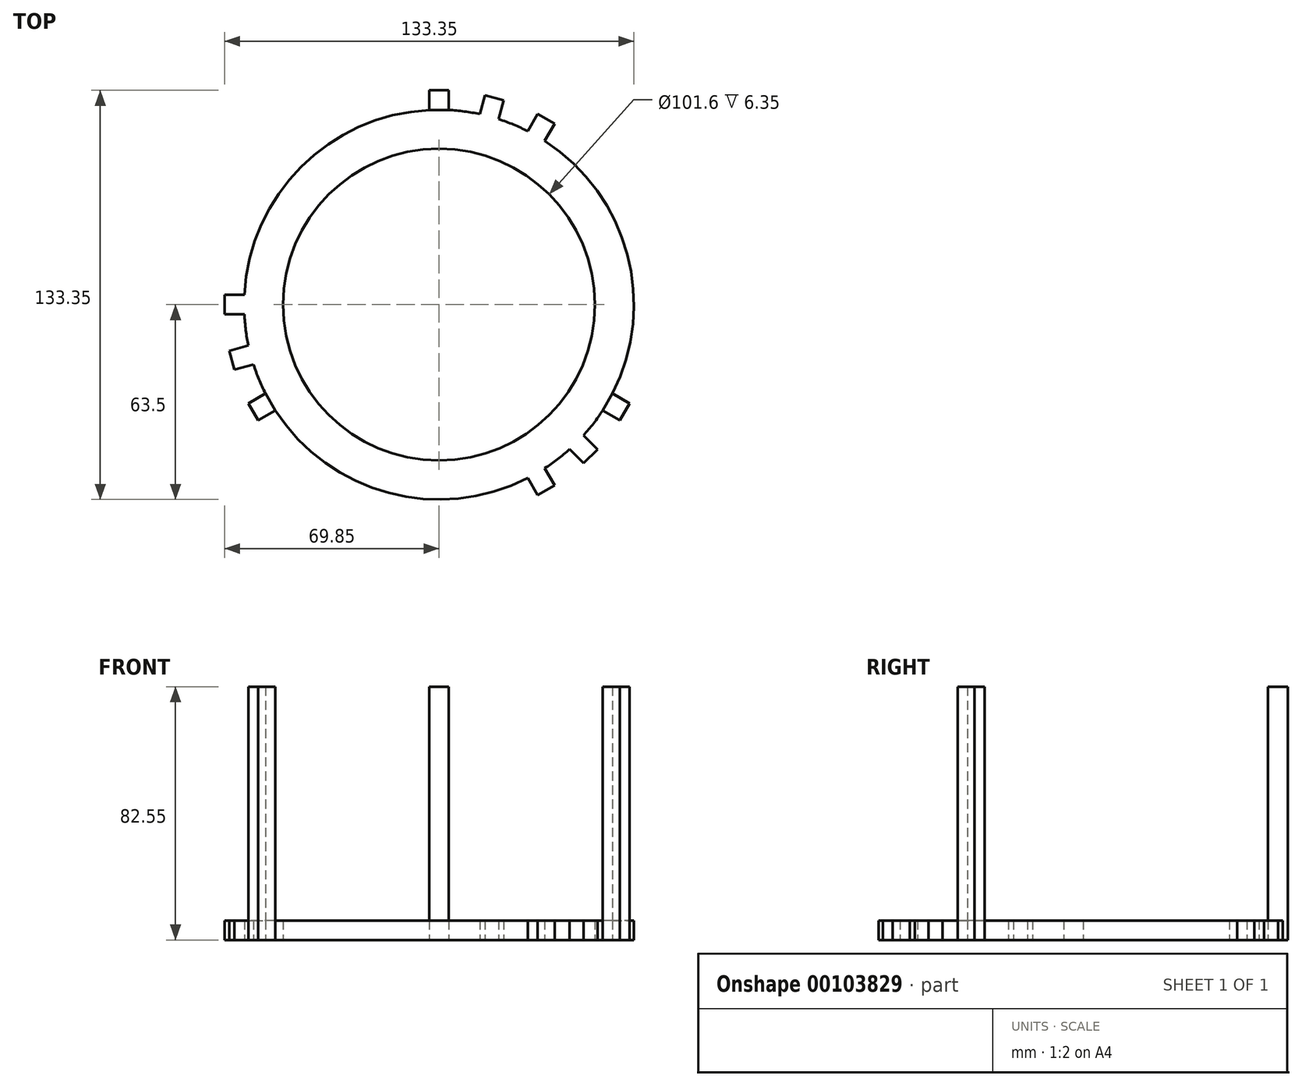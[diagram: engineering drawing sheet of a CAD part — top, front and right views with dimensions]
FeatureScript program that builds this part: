
annotation { "Feature Type Name" : "Feature", "Feature Type Description" : "" }
export const myFeature = defineFeature(function(context is Context, id is Id, definition is map)
    precondition{}
    {
        {
            var Q0;
            Q0=qCreatedBy(makeId("Top.planeOp"),FACE);
            var sketch = newSketch(context, id + "F0", { "sketchPlane" : qUnion([Q0])});
            skCircle(sketch, "E0", {"center": v(0, 0) * mm, "radius": 50.8 * mm});
            skCircle(sketch, "E1", {"center": v(0, 0) * mm, "radius": 63.5 * mm});
            skLineSegment(sketch, "E2.bottom", {"start": v(3.18, 69.85) * mm, "end": v(-3.17, 69.85) * mm});
            skLineSegment(sketch, "E2.top", {"start": v(3.18, 57.15) * mm, "end": v(-3.17, 57.15) * mm});
            skLineSegment(sketch, "E2.left", {"start": v(3.18, 69.85) * mm, "end": v(3.18, 57.15) * mm});
            skLineSegment(sketch, "E2.right", {"start": v(-3.17, 69.85) * mm, "end": v(-3.17, 57.15) * mm});
            skPoint(sketch, "E2.middle", {"position": v(0, 63.5) * mm});
            skLineSegment(sketch, "E3.1.0", {"start": v(21.15, 66.65) * mm, "end": v(15.01, 68.3) * mm});
            skLineSegment(sketch, "E3.1.1", {"start": v(21.15, 66.65) * mm, "end": v(17.86, 54.38) * mm});
            skLineSegment(sketch, "E3.1.2", {"start": v(17.86, 54.38) * mm, "end": v(11.72, 56.02) * mm});
            skLineSegment(sketch, "E3.1.3", {"start": v(15.01, 68.3) * mm, "end": v(11.72, 56.02) * mm});
            skLineSegment(sketch, "E3.2.0", {"start": v(37.67, 58.9) * mm, "end": v(32.18, 62.08) * mm});
            skLineSegment(sketch, "E3.2.1", {"start": v(37.67, 58.9) * mm, "end": v(31.32, 47.9) * mm});
            skLineSegment(sketch, "E3.2.2", {"start": v(31.32, 47.9) * mm, "end": v(25.83, 51.08) * mm});
            skLineSegment(sketch, "E3.2.3", {"start": v(32.18, 62.08) * mm, "end": v(25.83, 51.08) * mm});
            skLineSegment(sketch, "E3.anchor1", {"start": v(0, 0) * mm, "end": v(-3.17, 69.85) * mm, "construction": true});
            skLineSegment(sketch, "E3.anchor2", {"start": v(0, 0) * mm, "end": v(32.18, 62.08) * mm, "construction": true});
            skLineSegment(sketch, "E4.1.0", {"start": v(-69.85, 3.18) * mm, "end": v(-57.15, 3.18) * mm});
            skLineSegment(sketch, "E4.1.1", {"start": v(-69.85, 3.18) * mm, "end": v(-69.85, -3.17) * mm});
            skLineSegment(sketch, "E4.1.2", {"start": v(-57.15, 3.18) * mm, "end": v(-57.15, -3.17) * mm});
            skLineSegment(sketch, "E4.1.3", {"start": v(-69.85, -3.17) * mm, "end": v(-57.15, -3.17) * mm});
            skLineSegment(sketch, "E4.1.4", {"start": v(-68.3, -15.01) * mm, "end": v(-56.02, -11.72) * mm});
            skLineSegment(sketch, "E4.1.5", {"start": v(-68.3, -15.01) * mm, "end": v(-66.65, -21.15) * mm});
            skLineSegment(sketch, "E4.1.6", {"start": v(-56.02, -11.72) * mm, "end": v(-54.38, -17.86) * mm});
            skLineSegment(sketch, "E4.1.7", {"start": v(-66.65, -21.15) * mm, "end": v(-54.38, -17.86) * mm});
            skLineSegment(sketch, "E4.1.8", {"start": v(-62.08, -32.18) * mm, "end": v(-51.08, -25.83) * mm});
            skLineSegment(sketch, "E4.1.9", {"start": v(-62.08, -32.18) * mm, "end": v(-58.9, -37.67) * mm});
            skLineSegment(sketch, "E4.1.10", {"start": v(-58.9, -37.67) * mm, "end": v(-47.9, -31.32) * mm});
            skLineSegment(sketch, "E4.1.11", {"start": v(-51.08, -25.83) * mm, "end": v(-47.9, -31.32) * mm});
            skLineSegment(sketch, "E4.2.0", {"start": v(32.18, -62.08) * mm, "end": v(25.83, -51.08) * mm});
            skLineSegment(sketch, "E4.2.1", {"start": v(32.18, -62.08) * mm, "end": v(37.67, -58.9) * mm});
            skLineSegment(sketch, "E4.2.2", {"start": v(25.83, -51.08) * mm, "end": v(31.32, -47.9) * mm});
            skLineSegment(sketch, "E4.2.3", {"start": v(37.67, -58.9) * mm, "end": v(31.32, -47.9) * mm});
            skLineSegment(sketch, "E4.2.4", {"start": v(47.15, -51.64) * mm, "end": v(38.17, -42.66) * mm});
            skLineSegment(sketch, "E4.2.5", {"start": v(47.15, -51.64) * mm, "end": v(51.64, -47.15) * mm});
            skLineSegment(sketch, "E4.2.6", {"start": v(38.17, -42.66) * mm, "end": v(42.66, -38.17) * mm});
            skLineSegment(sketch, "E4.2.7", {"start": v(51.64, -47.15) * mm, "end": v(42.66, -38.17) * mm});
            skLineSegment(sketch, "E4.2.8", {"start": v(58.9, -37.67) * mm, "end": v(47.9, -31.32) * mm});
            skLineSegment(sketch, "E4.2.9", {"start": v(58.9, -37.67) * mm, "end": v(62.08, -32.18) * mm});
            skLineSegment(sketch, "E4.2.10", {"start": v(62.08, -32.18) * mm, "end": v(51.08, -25.83) * mm});
            skLineSegment(sketch, "E4.2.11", {"start": v(47.9, -31.32) * mm, "end": v(51.08, -25.83) * mm});
            skSolve(sketch);
        }
        {
            var Q0;
            Q0=makeQuery(id+"F0.imprint","IMPRINT",FACE,{"disambiguationData":[TD([[makeQuery(id+"F0.imprint","IMPRINT",EDGE,{"derivedFrom":sQuery(id+"F0.wireOp",EDGE,"E0")}),-1.0]])]});
            var Q1;
            {var subQ5=sQuery(id+"F0.wireOp",EDGE,"fd1a7b6d-0c8d-4171-9b3e-83a91182237e.1.1");Q1=makeQuery(id+"F0.imprint","IMPRINT",FACE,{"disambiguationData":[TD([[makeQuery(id+"F0.imprint","IMPRINT",EDGE,{"derivedFrom":subQ5}),1.0]])]});}
            var Q2;
            {var subQ5=sQuery(id+"F0.wireOp",EDGE,"fd1a7b6d-0c8d-4171-9b3e-83a91182237e.1.3");Q2=makeQuery(id+"F0.imprint","IMPRINT",FACE,{"disambiguationData":[TD([[makeQuery(id+"F0.imprint","IMPRINT",EDGE,{"derivedFrom":subQ5}),-1.0]])]});}
            var Q3;
            {var subQ5=sQuery(id+"F0.wireOp",EDGE,"E2.bottom");Q3=makeQuery(id+"F0.imprint","IMPRINT",FACE,{"disambiguationData":[TD([[makeQuery(id+"F0.imprint","IMPRINT",EDGE,{"derivedFrom":subQ5}),1.0]])]});}
            var Q4;
            {var subQ5=sQuery(id+"F0.wireOp",EDGE,"E2.top");Q4=makeQuery(id+"F0.imprint","IMPRINT",FACE,{"disambiguationData":[TD([[makeQuery(id+"F0.imprint","IMPRINT",EDGE,{"derivedFrom":subQ5}),-1.0]])]});}
            var Q5;
            {var subQ5=sQuery(id+"F0.wireOp",EDGE,"fd1a7b6d-0c8d-4171-9b3e-83a91182237e.2.1");Q5=makeQuery(id+"F0.imprint","IMPRINT",FACE,{"disambiguationData":[TD([[makeQuery(id+"F0.imprint","IMPRINT",EDGE,{"derivedFrom":subQ5}),1.0]])]});}
            var Q6;
            {var subQ5=sQuery(id+"F0.wireOp",EDGE,"fd1a7b6d-0c8d-4171-9b3e-83a91182237e.2.3");Q6=makeQuery(id+"F0.imprint","IMPRINT",FACE,{"disambiguationData":[TD([[makeQuery(id+"F0.imprint","IMPRINT",EDGE,{"derivedFrom":subQ5}),-1.0]])]});}
            var Q7;
            {var subQ5=sQuery(id+"F0.wireOp",EDGE,"E3.1.2");Q7=makeQuery(id+"F0.imprint","IMPRINT",FACE,{"disambiguationData":[TD([[makeQuery(id+"F0.imprint","IMPRINT",EDGE,{"derivedFrom":subQ5}),-1.0]])]});}
            var Q8;
            {var subQ5=sQuery(id+"F0.wireOp",EDGE,"E3.1.0");Q8=makeQuery(id+"F0.imprint","IMPRINT",FACE,{"disambiguationData":[TD([[makeQuery(id+"F0.imprint","IMPRINT",EDGE,{"derivedFrom":subQ5}),1.0]])]});}
            var Q9;
            {var subQ5=sQuery(id+"F0.wireOp",EDGE,"E3.2.0");Q9=makeQuery(id+"F0.imprint","IMPRINT",FACE,{"disambiguationData":[TD([[makeQuery(id+"F0.imprint","IMPRINT",EDGE,{"derivedFrom":subQ5}),1.0]])]});}
            var Q10;
            {var subQ5=sQuery(id+"F0.wireOp",EDGE,"E3.2.2");Q10=makeQuery(id+"F0.imprint","IMPRINT",FACE,{"disambiguationData":[TD([[makeQuery(id+"F0.imprint","IMPRINT",EDGE,{"derivedFrom":subQ5}),-1.0]])]});}
            var Q11;
            {var subQ5=sQuery(id+"F0.wireOp",EDGE,"E4.2.9");Q11=makeQuery(id+"F0.imprint","IMPRINT",FACE,{"disambiguationData":[TD([[makeQuery(id+"F0.imprint","IMPRINT",EDGE,{"derivedFrom":subQ5}),1.0]])]});}
            var Q12;
            {var subQ5=sQuery(id+"F0.wireOp",EDGE,"E4.2.11");Q12=makeQuery(id+"F0.imprint","IMPRINT",FACE,{"disambiguationData":[TD([[makeQuery(id+"F0.imprint","IMPRINT",EDGE,{"derivedFrom":subQ5}),-1.0]])]});}
            var Q13;
            {var subQ5=sQuery(id+"F0.wireOp",EDGE,"E4.2.5");Q13=makeQuery(id+"F0.imprint","IMPRINT",FACE,{"disambiguationData":[TD([[makeQuery(id+"F0.imprint","IMPRINT",EDGE,{"derivedFrom":subQ5}),1.0]])]});}
            var Q14;
            {var subQ5=sQuery(id+"F0.wireOp",EDGE,"E4.2.6");Q14=makeQuery(id+"F0.imprint","IMPRINT",FACE,{"disambiguationData":[TD([[makeQuery(id+"F0.imprint","IMPRINT",EDGE,{"derivedFrom":subQ5}),-1.0]])]});}
            var Q15;
            {var subQ5=sQuery(id+"F0.wireOp",EDGE,"E4.2.2");Q15=makeQuery(id+"F0.imprint","IMPRINT",FACE,{"disambiguationData":[TD([[makeQuery(id+"F0.imprint","IMPRINT",EDGE,{"derivedFrom":subQ5}),-1.0]])]});}
            var Q16;
            {var subQ5=sQuery(id+"F0.wireOp",EDGE,"E4.2.1");Q16=makeQuery(id+"F0.imprint","IMPRINT",FACE,{"disambiguationData":[TD([[makeQuery(id+"F0.imprint","IMPRINT",EDGE,{"derivedFrom":subQ5}),1.0]])]});}
            var Q17;
            {var subQ5=sQuery(id+"F0.wireOp",EDGE,"E4.1.9");Q17=makeQuery(id+"F0.imprint","IMPRINT",FACE,{"disambiguationData":[TD([[makeQuery(id+"F0.imprint","IMPRINT",EDGE,{"derivedFrom":subQ5}),1.0]])]});}
            var Q18;
            {var subQ5=sQuery(id+"F0.wireOp",EDGE,"E4.1.5");Q18=makeQuery(id+"F0.imprint","IMPRINT",FACE,{"disambiguationData":[TD([[makeQuery(id+"F0.imprint","IMPRINT",EDGE,{"derivedFrom":subQ5}),1.0]])]});}
            var Q19;
            {var subQ5=sQuery(id+"F0.wireOp",EDGE,"E4.1.1");Q19=makeQuery(id+"F0.imprint","IMPRINT",FACE,{"disambiguationData":[TD([[makeQuery(id+"F0.imprint","IMPRINT",EDGE,{"derivedFrom":subQ5}),1.0]])]});}
            var Q20;
            {var subQ5=sQuery(id+"F0.wireOp",EDGE,"E4.1.2");Q20=makeQuery(id+"F0.imprint","IMPRINT",FACE,{"disambiguationData":[TD([[makeQuery(id+"F0.imprint","IMPRINT",EDGE,{"derivedFrom":subQ5}),-1.0]])]});}
            var Q21;
            {var subQ5=sQuery(id+"F0.wireOp",EDGE,"E4.1.6");Q21=makeQuery(id+"F0.imprint","IMPRINT",FACE,{"disambiguationData":[TD([[makeQuery(id+"F0.imprint","IMPRINT",EDGE,{"derivedFrom":subQ5}),-1.0]])]});}
            var Q22;
            {var subQ5=sQuery(id+"F0.wireOp",EDGE,"E4.1.11");Q22=makeQuery(id+"F0.imprint","IMPRINT",FACE,{"disambiguationData":[TD([[makeQuery(id+"F0.imprint","IMPRINT",EDGE,{"derivedFrom":subQ5}),-1.0]])]});}
            extrude(context, id + "F1", {"entities" : qUnion([Q0, Q1, Q2, Q3, Q4, Q5, Q6, Q7, Q8, Q9, Q10, Q11, Q12, Q13, Q14, Q15, Q16, Q17, Q18, Q19, Q20, Q21, Q22]), "depth" : 6.35 * mm});
        }
        {
            var Q0;
            Q0=makeQuery(id+"F1.opExtrude","CAP_FACE",FACE,{"disambiguationData":[OSD([sQuery(id+"F0.wireOp",EDGE,"E0"),sQuery(id+"F0.wireOp",EDGE,"E1"),sQuery(id+"F0.wireOp",EDGE,"E2.bottom"),sQuery(id+"F0.wireOp",EDGE,"E2.left"),sQuery(id+"F0.wireOp",EDGE,"E2.right"),sQuery(id+"F0.wireOp",EDGE,"E3.1.0"),sQuery(id+"F0.wireOp",EDGE,"E3.1.1"),sQuery(id+"F0.wireOp",EDGE,"E3.1.3"),sQuery(id+"F0.wireOp",EDGE,"E3.2.0"),sQuery(id+"F0.wireOp",EDGE,"E3.2.1"),sQuery(id+"F0.wireOp",EDGE,"E3.2.3"),sQuery(id+"F0.wireOp",EDGE,"E4.1.0"),sQuery(id+"F0.wireOp",EDGE,"E4.1.1"),sQuery(id+"F0.wireOp",EDGE,"E4.1.3"),sQuery(id+"F0.wireOp",EDGE,"E4.1.4"),sQuery(id+"F0.wireOp",EDGE,"E4.1.5"),sQuery(id+"F0.wireOp",EDGE,"E4.1.7"),sQuery(id+"F0.wireOp",EDGE,"E4.1.8"),sQuery(id+"F0.wireOp",EDGE,"E4.1.9"),sQuery(id+"F0.wireOp",EDGE,"E4.1.10"),sQuery(id+"F0.wireOp",EDGE,"E4.2.0"),sQuery(id+"F0.wireOp",EDGE,"E4.2.1"),sQuery(id+"F0.wireOp",EDGE,"E4.2.3"),sQuery(id+"F0.wireOp",EDGE,"E4.2.4"),sQuery(id+"F0.wireOp",EDGE,"E4.2.5"),sQuery(id+"F0.wireOp",EDGE,"E4.2.7"),sQuery(id+"F0.wireOp",EDGE,"E4.2.8"),sQuery(id+"F0.wireOp",EDGE,"E4.2.9"),sQuery(id+"F0.wireOp",EDGE,"E4.2.10")])],"isStart":false});
            var sketch = newSketch(context, id + "F2", { "sketchPlane" : qUnion([Q0])});
            skLineSegment(sketch, "E5.bottom", {"start": v(-3.17, 69.85) * mm, "end": v(3.18, 69.85) * mm});
            skLineSegment(sketch, "E5.top", {"start": v(-3.17, 63.42) * mm, "end": v(3.18, 63.42) * mm});
            skLineSegment(sketch, "E5.left", {"start": v(-3.17, 69.85) * mm, "end": v(-3.17, 63.42) * mm});
            skLineSegment(sketch, "E5.right", {"start": v(3.18, 69.85) * mm, "end": v(3.18, 63.42) * mm});
            skPoint(sketch, "E6.center", {"position": v(0, 0) * mm});
            skLineSegment(sketch, "E6.anchor1", {"start": v(0, 0) * mm, "end": v(-3.17, 69.85) * mm, "construction": true});
            skLineSegment(sketch, "E7.1.4", {"start": v(-62.08, -32.18) * mm, "end": v(-56.51, -28.96) * mm});
            skLineSegment(sketch, "E7.1.5", {"start": v(-58.9, -37.67) * mm, "end": v(-62.08, -32.18) * mm});
            skLineSegment(sketch, "E7.1.6", {"start": v(-58.9, -37.67) * mm, "end": v(-53.34, -34.46) * mm});
            skLineSegment(sketch, "E7.1.7", {"start": v(-53.34, -34.46) * mm, "end": v(-56.51, -28.96) * mm});
            skLineSegment(sketch, "E7.2.4", {"start": v(58.9, -37.67) * mm, "end": v(53.34, -34.46) * mm});
            skLineSegment(sketch, "E7.2.5", {"start": v(62.08, -32.18) * mm, "end": v(58.9, -37.67) * mm});
            skLineSegment(sketch, "E7.2.6", {"start": v(62.08, -32.18) * mm, "end": v(56.51, -28.96) * mm});
            skLineSegment(sketch, "E7.2.7", {"start": v(56.51, -28.96) * mm, "end": v(53.34, -34.46) * mm});
            skSolve(sketch);
        }
        {
            var Q0;
            Q0=makeQuery(id+"F2.imprint","IMPRINT",FACE,{"disambiguationData":[TD([[makeQuery(id+"F2.imprint","IMPRINT",EDGE,{"derivedFrom":sQuery(id+"F2.wireOp",EDGE,"E5.bottom")}),1.0]])]});
            var Q1;
            Q1=makeQuery(id+"F2.imprint","IMPRINT",FACE,{"disambiguationData":[TD([[makeQuery(id+"F2.imprint","IMPRINT",EDGE,{"derivedFrom":sQuery(id+"F2.wireOp",EDGE,"E6.1.0")}),1.0]])]});
            var Q2;
            Q2=makeQuery(id+"F2.imprint","IMPRINT",FACE,{"disambiguationData":[TD([[makeQuery(id+"F2.imprint","IMPRINT",EDGE,{"derivedFrom":sQuery(id+"F2.wireOp",EDGE,"E7.2.4")}),-1.0]])]});
            var Q3;
            Q3=makeQuery(id+"F2.imprint","IMPRINT",FACE,{"disambiguationData":[TD([[makeQuery(id+"F2.imprint","IMPRINT",EDGE,{"derivedFrom":sQuery(id+"F2.wireOp",EDGE,"E7.2.0")}),1.0]])]});
            var Q4;
            Q4=makeQuery(id+"F2.imprint","IMPRINT",FACE,{"disambiguationData":[TD([[makeQuery(id+"F2.imprint","IMPRINT",EDGE,{"derivedFrom":sQuery(id+"F2.wireOp",EDGE,"E7.1.4")}),-1.0]])]});
            var Q5;
            Q5=makeQuery(id+"F2.imprint","IMPRINT",FACE,{"disambiguationData":[TD([[makeQuery(id+"F2.imprint","IMPRINT",EDGE,{"derivedFrom":sQuery(id+"F2.wireOp",EDGE,"E7.1.0")}),1.0]])]});
            extrude(context, id + "F3", {"entities" : qUnion([Q0, Q1, Q2, Q3, Q4, Q5]), "operationType" : NewBodyOperationType.ADD, "depth" : 76.2 * mm});
        }
    });
